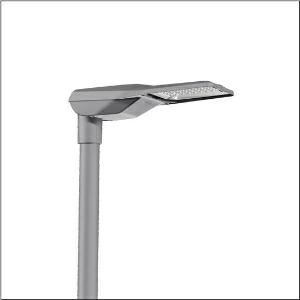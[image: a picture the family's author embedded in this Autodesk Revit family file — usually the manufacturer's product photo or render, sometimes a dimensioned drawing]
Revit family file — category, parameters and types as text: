
# Revit family: streetlight_sl_21_mini___pl52_5xe6h43a08gb_f715
name_source: partatom
category: Lighting Fixtures
units: mm (PartAtom-declared; Revit-internal decimal feet)

## family parameters
Cut with Voids When Loaded = No
Host = Face
Light Source = No
Part Type = Normal
Room Calculation Point = No
Round Connector Dimension = Use Diameter
Shared = No

## types (1)
- --- (1 x LED, 6080 lm, 40.4 W, 4000K)
    Apparent Load = 40 VA
    CIE Flux Codes = 27 59 98 100 100
    Color Rendering = 70
    Color Temperature = 4000K
    Default Elevation = 1800 mm
    Description = Streetlight SL 21 mini, mast luminaire, primary light control with lens, of PMMA, primary optical cover: cover, of toughened safety glass, transparent, light distribution: PL52, light emission: direct distribution, primary light characteristic: asymmetric, installation type: post-top, side-entry, LED, 3G 1.5mm², High Power LED, rated luminous flux: 6.080lm, luminous efficacy: 151lm/W, light colour: 740, colour temperature: 4000K, control: overheat protection, constant luminous flux control, time-dependent luminous flux control, flexible luminous flux parameterisation, mains connection: 230..240V, AC, 50/60Hz, connection cable pre-assembled, cable length: 6,5m, wiring characteristics: H07RN-F, start of lifetime: 40W, end of service life: 41W, reduction: 19W, luminaire housing, of diecast aluminium, powder-coated, Siteco® metallic grey (DB 702S), corrosivity category C5 mid according to DIN EN ISO 12944, please order mast flange separately, inclination adjustable: 0°, 5°, 10°, 15°, sealing non-destructively replaceable, multi-level sealing system, length: 628mm, width: 235mm, height: 110mm, mast flange for spigot size: 42mm (side-entry): 5XC10008XM4, 60/48mm (side-entry/post-top): 5XC10108XM2, 76/60mm (side-entry/post-top): 5XC10108XM1, protection rating (complete): IP66, insulation class (complete): insulation class II (safety insulation), certification: CE, ENEC, ENEC+, VDE, impact resistance: IK09, permissible operating ambient temperature for outdoor applications: -40..+50°C, standard-compliant lighting for roads and squares, packaging unit: 1 piece

Light Distribution: PL52
    Height = 110 mm
    Lamp = 1 x LED
    Lamp Light Flux = 6080 lm
    Lamp Power = 40.4 W
    Lamp count = 1
    Length = 625 mm
    Luminous efficacy = 151 lm/W
    Manufacturer = Siteco
    ModVariant = No
    Model = 5XE6H43A08GB
    Number of Poles = 1
    OnlyDefault = Yes
    Power Factor = 1
    Product Name = Streetlight SL 21 mini | PL52
    Product group = mast luminaire | pylon top
    ProductGroupID = 6100
    Protection Class = Protection class II
    Protection Degree = IP 66
    RLX_Detail_Level = 1
    RLX_Emergency_Light_Flux = 0 lm
    RLX_Emergency_Type = 0
    RLX_Emergency_Type_DB = No
    RlxData = <blob elided: 103457 chars, md5=e9ca261d>
    Socket = socket
    Standby Power = 0 W
    System Light Flux = 6080 lm
    System Power = 40 W
    Type Comments = factory setting: luminous flux: 100 % | Output Level: 100 % | 812 mA
    Type Image = l_1003519.jpg
    URL = http://relux.com
    VarID = @adj_123867
    Voltage = 0 V
    Weight = 0.00 kg
    Width = 234 mm

## geometry (parser evidence)
native form markers: Blend x4, Sweep x11
no freeform markers — native parametric forms only
